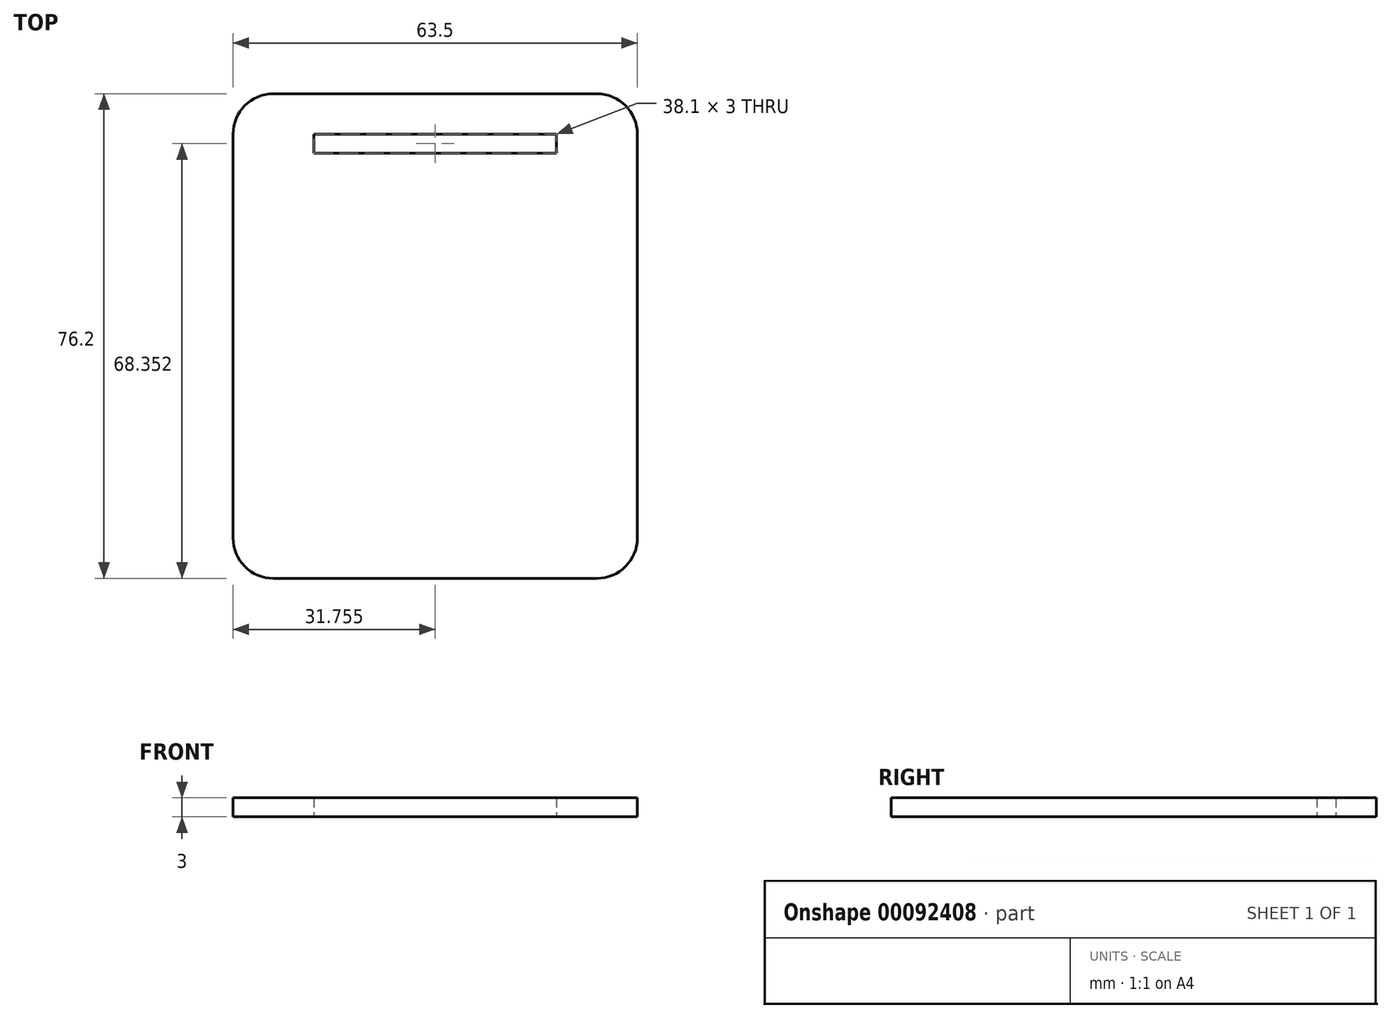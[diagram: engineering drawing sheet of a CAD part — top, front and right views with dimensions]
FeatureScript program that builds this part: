
annotation { "Feature Type Name" : "Feature", "Feature Type Description" : "" }
export const myFeature = defineFeature(function(context is Context, id is Id, definition is map)
    precondition{}
    {
        {
            var Q0;
            Q0=qCreatedBy(makeId("Top.planeOp"),FACE);
            var sketch = newSketch(context, id + "F0", { "sketchPlane" : qUnion([Q0])});
            skLineSegment(sketch, "E0.bottom", {"start": v(-25.2, 43.83) * mm, "end": v(25.6, 43.83) * mm});
            skLineSegment(sketch, "E0.top", {"start": v(-25.2, -32.37) * mm, "end": v(25.6, -32.37) * mm});
            skLineSegment(sketch, "E0.left", {"start": v(-31.55, 37.48) * mm, "end": v(-31.55, -26.02) * mm});
            skLineSegment(sketch, "E0.right", {"start": v(31.95, 37.48) * mm, "end": v(31.95, -26.02) * mm});
            skLineSegment(sketch, "E1.bottom", {"start": v(-18.85, 37.48) * mm, "end": v(19.25, 37.48) * mm});
            skLineSegment(sketch, "E1.top", {"start": v(-18.85, 34.48) * mm, "end": v(19.25, 34.48) * mm});
            skLineSegment(sketch, "E1.left", {"start": v(-18.85, 37.48) * mm, "end": v(-18.85, 34.48) * mm});
            skLineSegment(sketch, "E1.right", {"start": v(19.25, 37.48) * mm, "end": v(19.25, 34.48) * mm});
            skPoint(sketch, "E2.visualSharp", {"position": v(31.95, 43.83) * mm});
            skArc(sketch, "E2.filletArc", {"start": v(31.95, 37.48) * mm, "mid": v(30.1, 41.97) * mm, "end": v(25.6, 43.83) * mm});
            skPoint(sketch, "E3.visualSharp", {"position": v(-31.55, 43.83) * mm});
            skArc(sketch, "E3.filletArc", {"start": v(-25.2, 43.83) * mm, "mid": v(-29.69, 41.97) * mm, "end": v(-31.55, 37.48) * mm});
            skPoint(sketch, "E4.visualSharp", {"position": v(-31.55, -32.37) * mm});
            skArc(sketch, "E4.filletArc", {"start": v(-31.55, -26.02) * mm, "mid": v(-29.69, -30.5) * mm, "end": v(-25.2, -32.37) * mm});
            skPoint(sketch, "E5.visualSharp", {"position": v(31.95, -32.37) * mm});
            skArc(sketch, "E5.filletArc", {"start": v(25.6, -32.37) * mm, "mid": v(30.1, -30.5) * mm, "end": v(31.95, -26.02) * mm});
            skSolve(sketch);
        }
        {
            var Q0;
            Q0=makeQuery(id+"F0.imprint","IMPRINT",FACE,{"disambiguationData":[TD([[makeQuery(id+"F0.imprint","IMPRINT",EDGE,{"derivedFrom":sQuery(id+"F0.wireOp",EDGE,"E0.bottom")}),-1.0]])]});
            extrude(context, id + "F1", {"entities" : qUnion([Q0]), "depth" : 3 * mm});
        }
    });
